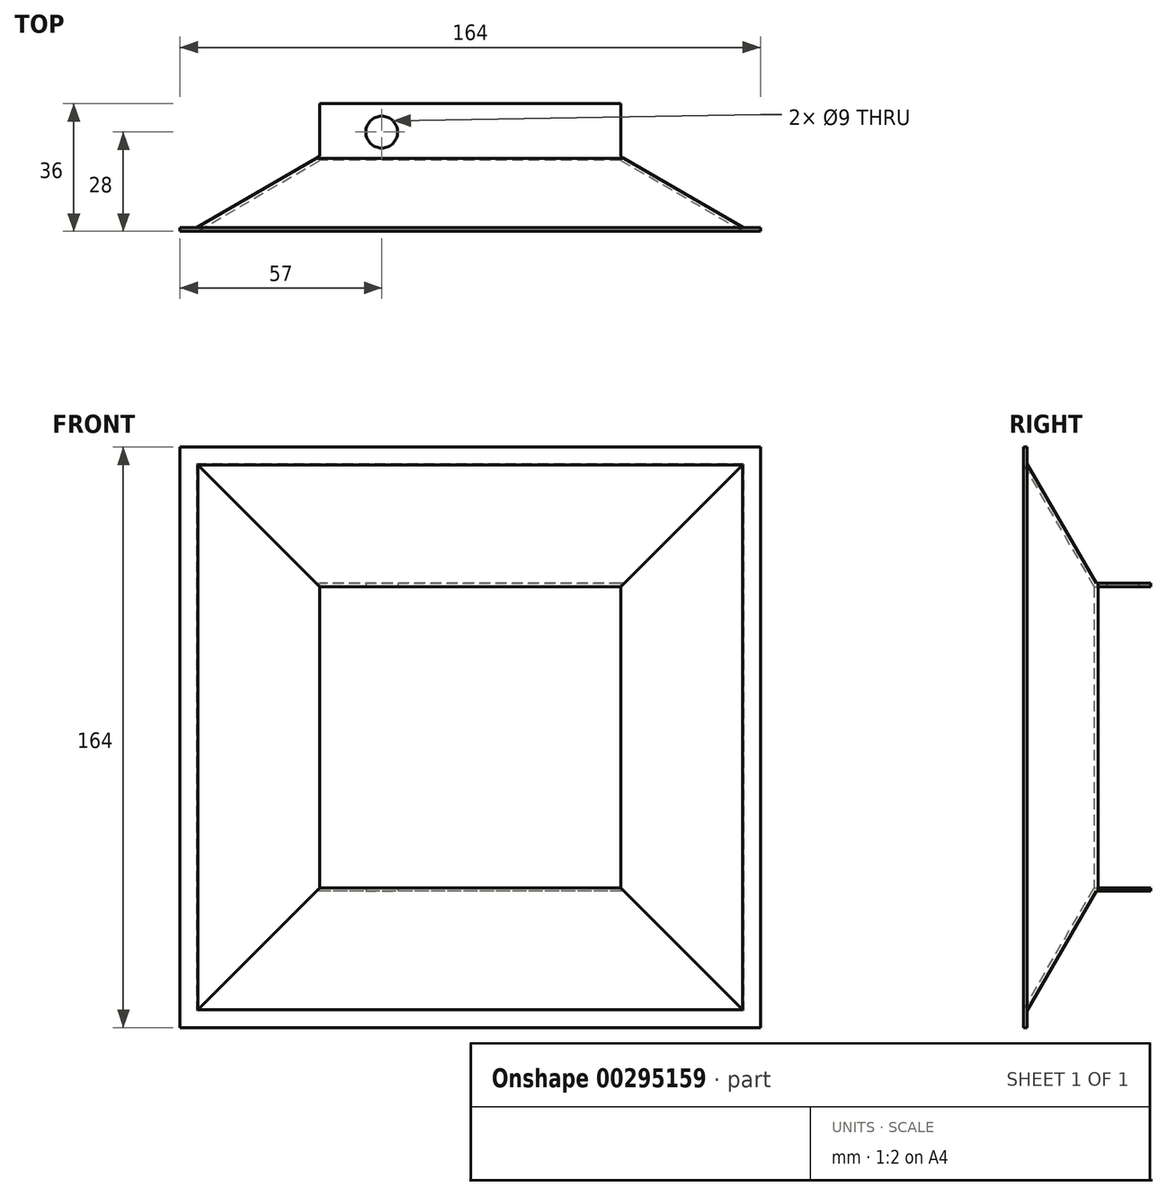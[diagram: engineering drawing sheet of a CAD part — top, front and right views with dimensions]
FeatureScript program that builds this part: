
annotation { "Feature Type Name" : "Feature", "Feature Type Description" : "" }
export const myFeature = defineFeature(function(context is Context, id is Id, definition is map)
    precondition{}
    {
        {
            var Q0;
            Q0=qCreatedBy(makeId("Front.planeOp"),FACE);
            var sketch = newSketch(context, id + "F0", { "sketchPlane" : qUnion([Q0])});
            skLineSegment(sketch, "E0.bottom", {"start": v(82, 82) * mm, "end": v(-82, 82) * mm});
            skLineSegment(sketch, "E0.top", {"start": v(82, -82) * mm, "end": v(-82, -82) * mm});
            skLineSegment(sketch, "E0.left", {"start": v(82, 82) * mm, "end": v(82, -82) * mm});
            skLineSegment(sketch, "E0.right", {"start": v(-82, 82) * mm, "end": v(-82, -82) * mm});
            skPoint(sketch, "E0.middle", {"position": v(0, 0) * mm});
            skLineSegment(sketch, "E1.0", {"start": v(77, 77) * mm, "end": v(-77, 77) * mm});
            skLineSegment(sketch, "E1.1", {"start": v(77, 77) * mm, "end": v(77, -77) * mm});
            skLineSegment(sketch, "E1.2", {"start": v(77, -77) * mm, "end": v(-77, -77) * mm});
            skLineSegment(sketch, "E1.3", {"start": v(-77, 77) * mm, "end": v(-77, -77) * mm});
            skSolve(sketch);
        }
        {
            var Q0;
            Q0=makeQuery(id+"F0.imprint","IMPRINT",FACE,{"disambiguationData":[TD([[makeQuery(id+"F0.imprint","IMPRINT",EDGE,{"derivedFrom":sQuery(id+"F0.wireOp",EDGE,"E1.0")}),1.0]])]});
            cPlane(context, id + "F1", {"entities" : qUnion([Q0]), "cplaneType" : CPlaneType.OFFSET, "offset" : 20 * mm, "oppositeDirection" : true, "width" : 150 * mm, "height" : 150 * mm});
        }
        {
            var Q0;
            Q0=qCreatedBy(id+"F1.planeOp",FACE);
            var sketch = newSketch(context, id + "F2", { "sketchPlane" : qUnion([Q0])});
            skPoint(sketch, "E2", {"position": v(0, 0) * mm});
            skLineSegment(sketch, "E3.bottom", {"start": v(42.5, 42.5) * mm, "end": v(-42.5, 42.5) * mm});
            skLineSegment(sketch, "E3.top", {"start": v(42.5, -42.5) * mm, "end": v(-42.5, -42.5) * mm});
            skLineSegment(sketch, "E3.left", {"start": v(42.5, 42.5) * mm, "end": v(42.5, -42.5) * mm});
            skLineSegment(sketch, "E3.right", {"start": v(-42.5, 42.5) * mm, "end": v(-42.5, -42.5) * mm});
            skSolve(sketch);
        }
        {
            var Q0;
            Q0=qCreatedBy(id+"F1.planeOp",FACE);
            cPlane(context, id + "F3", {"entities" : qUnion([Q0]), "cplaneType" : CPlaneType.OFFSET, "offset" : 16 * mm, "oppositeDirection" : true, "width" : 150 * mm, "height" : 150 * mm});
        }
        {
            var Q0;
            Q0=qCreatedBy(id+"F3.planeOp",FACE);
            var sketch = newSketch(context, id + "F4", { "sketchPlane" : qUnion([Q0])});
            skLineSegment(sketch, "E4.0.0", {"start": v(-42.5, -42.5) * mm, "end": v(42.5, -42.5) * mm});
            skLineSegment(sketch, "E4.0.1", {"start": v(42.5, -42.5) * mm, "end": v(42.5, 42.5) * mm});
            skLineSegment(sketch, "E4.0.2", {"start": v(42.5, 42.5) * mm, "end": v(-42.5, 42.5) * mm});
            skLineSegment(sketch, "E4.0.3", {"start": v(-42.5, 42.5) * mm, "end": v(-42.5, -42.5) * mm});
            skSolve(sketch);
        }
        {
            var Q0;
            Q0=makeQuery(id+"F0.imprint","IMPRINT",FACE,{"disambiguationData":[TD([[makeQuery(id+"F0.imprint","IMPRINT",EDGE,{"derivedFrom":sQuery(id+"F0.wireOp",EDGE,"E1.0")}),1.0]])]});
            var Q1;
            Q1=makeQuery(id+"F2.imprint","IMPRINT",FACE,{"disambiguationData":[TD([[makeQuery(id+"F2.imprint","IMPRINT",EDGE,{"derivedFrom":sQuery(id+"F2.wireOp",EDGE,"E3.bottom")}),1.0]])]});
            loft(context, id + "F5", {"sheetProfilesArray" : [{ "sheetProfileEntities" : qUnion([Q0]) }, { "sheetProfileEntities" : qUnion([Q1]) }]});
        }
        {
            var Q1;
            Q1=makeQuery(id+"F2.imprint","IMPRINT",FACE,{"disambiguationData":[TD([[makeQuery(id+"F2.imprint","IMPRINT",EDGE,{"derivedFrom":sQuery(id+"F2.wireOp",EDGE,"E3.bottom")}),1.0]])]});
            var Q2;
            Q2=makeQuery(id+"F4.imprint","IMPRINT",FACE,{"disambiguationData":[TD([[makeQuery(id+"F4.imprint","IMPRINT",EDGE,{"derivedFrom":sQuery(id+"F4.wireOp",EDGE,"E4.0.0")}),1.0]])]});
            loft(context, id + "F6", {"operationType" : NewBodyOperationType.ADD, "sheetProfilesArray" : [{ "sheetProfileEntities" : qUnion([Q1]) }, { "sheetProfileEntities" : qUnion([Q2]) }]});
        }
        {
            var Q0;
            Q0=makeQuery(id+"F5.opLoft","CAP_FACE",FACE,{"disambiguationData":[OSD([makeQuery(id+"F0.imprint","IMPRINT",FACE,{"disambiguationData":[TD([[makeQuery(id+"F0.imprint","IMPRINT",EDGE,{"derivedFrom":sQuery(id+"F0.wireOp",EDGE,"E1.0")}),1.0]])]})])],"isStart":true});
            var Q1;
            Q1=makeQuery(id+"F6.opLoft","CAP_FACE",FACE,{"disambiguationData":[OSD([makeQuery(id+"F4.imprint","IMPRINT",FACE,{"disambiguationData":[TD([[makeQuery(id+"F4.imprint","IMPRINT",EDGE,{"derivedFrom":sQuery(id+"F4.wireOp",EDGE,"E4.0.0")}),1.0]])]})])],"isStart":true});
            var Q2;
            Q2=makeQuery(id+"F6.opLoft","SWEPT_FACE",FACE,{"disambiguationData":[OSD([sQuery(id+"F2.wireOp",EDGE,"E3.bottom"),sQuery(id+"F2.wireOp",EDGE,"E3.top"),sQuery(id+"F2.wireOp",EDGE,"E3.right"),sQuery(id+"F4.wireOp",EDGE,"E4.0.0"),sQuery(id+"F4.wireOp",EDGE,"E4.0.2"),sQuery(id+"F4.wireOp",EDGE,"E4.0.3")])]});
            var Q3;
            Q3=makeQuery(id+"F6.opLoft","SWEPT_FACE",FACE,{"disambiguationData":[OSD([sQuery(id+"F2.wireOp",EDGE,"E3.bottom"),sQuery(id+"F2.wireOp",EDGE,"E3.top"),sQuery(id+"F2.wireOp",EDGE,"E3.left"),sQuery(id+"F4.wireOp",EDGE,"E4.0.0"),sQuery(id+"F4.wireOp",EDGE,"E4.0.1"),sQuery(id+"F4.wireOp",EDGE,"E4.0.2")])]});
            shell(context, id + "F7", {"entities" : qUnion([Q0, Q1, Q2, Q3]), "thickness" : 1 * mm, "oppositeDirection" : true});
        }
        {
            var Q0;
            Q0=makeQuery(id+"F0.imprint","IMPRINT",FACE,{"disambiguationData":[TD([[makeQuery(id+"F0.imprint","IMPRINT",EDGE,{"derivedFrom":sQuery(id+"F0.wireOp",EDGE,"E0.bottom")}),1.0]])]});
            extrude(context, id + "F8", {"entities" : qUnion([Q0]), "operationType" : NewBodyOperationType.ADD, "oppositeDirection" : true, "depth" : 1 * mm});
        }
        {
            var Q0;
            Q0=qCreatedBy(makeId("Top.planeOp"),FACE);
            var sketch = newSketch(context, id + "F9", { "sketchPlane" : qUnion([Q0])});
            skCircle(sketch, "E5", {"center": v(-25, 28) * mm, "radius": 4.5 * mm});
            skCircle(sketch, "E6.MirrorC", {"center": v(25, 28) * mm, "radius": 4.5 * mm});
            skSolve(sketch);
        }
        {
            var Q0;
            Q0=makeQuery(id+"F9.imprint","IMPRINT",FACE,{"disambiguationData":[TD([[makeQuery(id+"F9.imprint","IMPRINT",EDGE,{"derivedFrom":sQuery(id+"F9.wireOp",EDGE,"E6.MirrorC")}),-1.0]])]});
            var Q1;
            Q1=makeQuery(id+"F9.imprint","IMPRINT",FACE,{"disambiguationData":[TD([[makeQuery(id+"F9.imprint","IMPRINT",EDGE,{"derivedFrom":sQuery(id+"F9.wireOp",EDGE,"E5")}),1.0]])]});
            extrude(context, id + "F10", {"entities" : qUnion([Q0, Q1]), "operationType" : NewBodyOperationType.REMOVE, "endBound" : BoundingType.SYMMETRIC, "depth" : 114.4 * mm});
        }
    });
